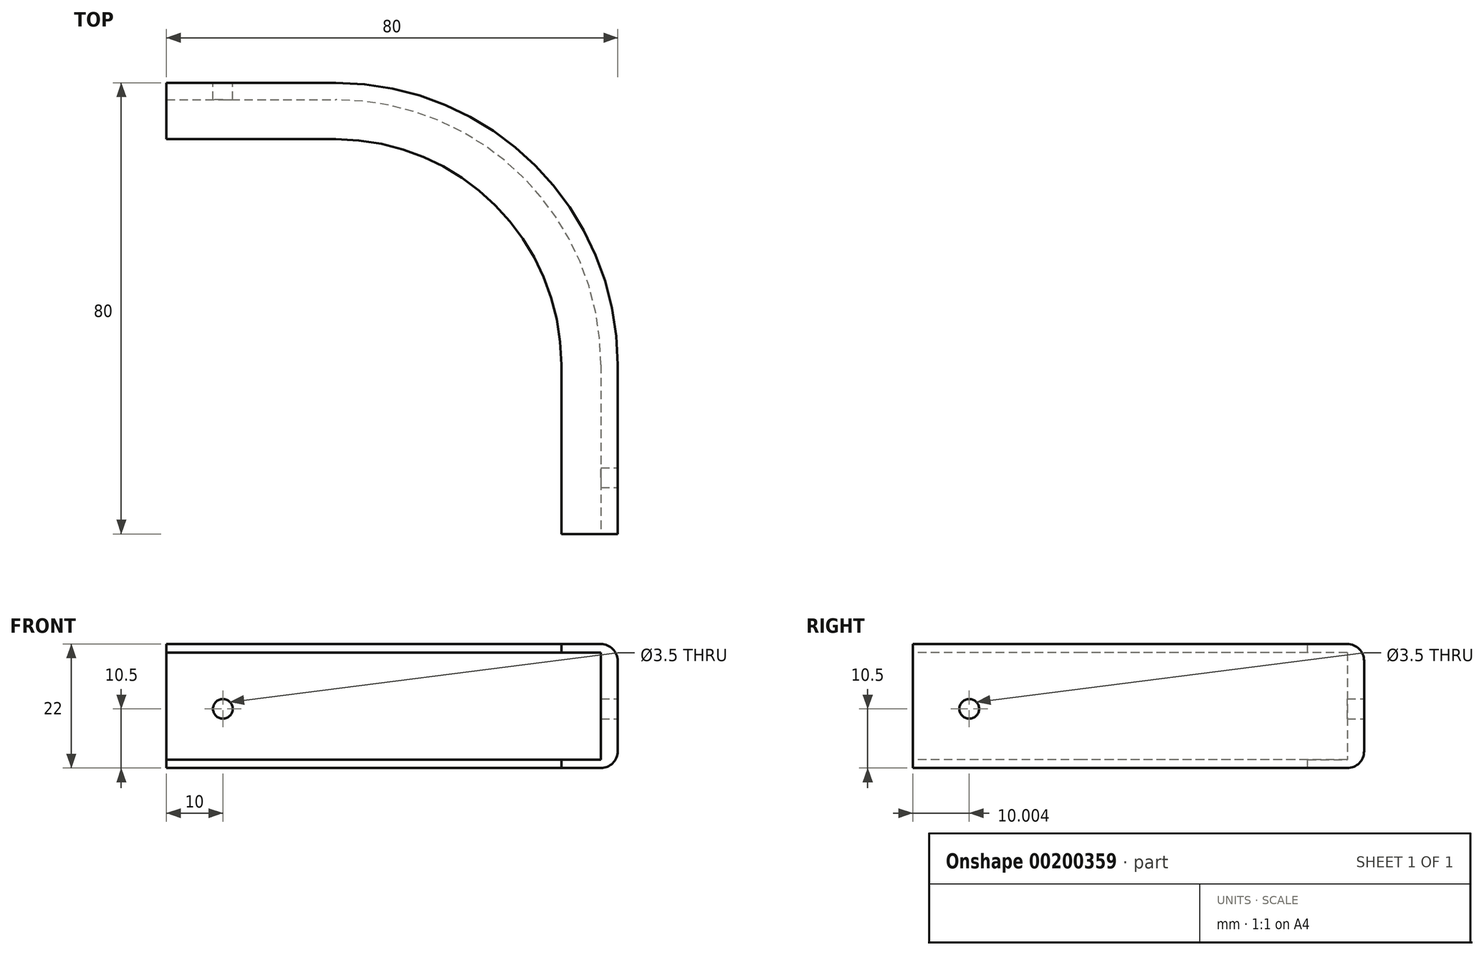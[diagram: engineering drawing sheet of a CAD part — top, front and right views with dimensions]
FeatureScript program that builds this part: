
annotation { "Feature Type Name" : "Feature", "Feature Type Description" : "" }
export const myFeature = defineFeature(function(context is Context, id is Id, definition is map)
    precondition{}
    {
        {
            var Q0;
            Q0=qCreatedBy(makeId("Right.planeOp"),FACE);
            var sketch = newSketch(context, id + "F0", { "sketchPlane" : qUnion([Q0])});
            skPoint(sketch, "E0.0", {"position": v(1.08, 10) * mm});
            skPoint(sketch, "E1.0", {"position": v(1.08, -9) * mm});
            skLineSegment(sketch, "E2", {"start": v(1.08, 10) * mm, "end": v(-5.92, 10) * mm});
            skLineSegment(sketch, "E3", {"start": v(-5.92, 10) * mm, "end": v(-5.92, 11.5) * mm});
            skLineSegment(sketch, "E4", {"start": v(-5.92, 11.5) * mm, "end": v(1.08, 11.5) * mm});
            skLineSegment(sketch, "E5", {"start": v(4.08, 8.5) * mm, "end": v(4.08, -7.5) * mm});
            skLineSegment(sketch, "E6", {"start": v(1.08, -10.5) * mm, "end": v(-5.92, -10.5) * mm});
            skLineSegment(sketch, "E7", {"start": v(-5.92, -10.5) * mm, "end": v(-5.92, -9) * mm});
            skLineSegment(sketch, "E8", {"start": v(-5.92, -9) * mm, "end": v(1.08, -9) * mm});
            skLineSegment(sketch, "E9", {"start": v(1.08, 10) * mm, "end": v(1.08, -9) * mm});
            skPoint(sketch, "E10.visualSharp", {"position": v(4.08, 11.5) * mm});
            skArc(sketch, "E10.filletArc", {"start": v(4.08, 8.5) * mm, "mid": v(3.2, 10.62) * mm, "end": v(1.08, 11.5) * mm});
            skPoint(sketch, "E11.visualSharp", {"position": v(4.08, -10.5) * mm});
            skArc(sketch, "E11.filletArc", {"start": v(1.08, -10.5) * mm, "mid": v(3.2, -9.62) * mm, "end": v(4.08, -7.5) * mm});
            skSolve(sketch);
        }
        {
            var Q0;
            Q0=qCreatedBy(makeId("Top.planeOp"),FACE);
            var sketch = newSketch(context, id + "F1", { "sketchPlane" : qUnion([Q0])});
            skPoint(sketch, "E12.0", {"position": v(0, -5.92) * mm});
            skLineSegment(sketch, "E13", {"start": v(0, -5.92) * mm, "end": v(30, -5.92) * mm});
            skArc(sketch, "E14", {"start": v(30, -5.92) * mm, "mid": v(58.28, -17.63) * mm, "end": v(70, -45.92) * mm});
            skLineSegment(sketch, "E15", {"start": v(70, -45.92) * mm, "end": v(70, -75.92) * mm});
            skSolve(sketch);
        }
        {
            var Q0;
            Q0 = qSketchRegion(id + "F0", true);
            var Q1;
            Q1 = qConstructionFilter(qBodyType(qCreatedBy(id + "F1" ,EDGE), BodyType.WIRE), ConstructionObject.NO);
            sweep(context, id + "F2", {"profiles" : qUnion([Q0]), "path" : qUnion([Q1])});
        }
        {
            var Q0;
            Q0=makeQuery(id+"F2.opSweep","SWEPT_FACE",FACE,{"disambiguationData":[OSD([sQuery(id+"F0.wireOp",EDGE,"E5"),sQuery(id+"F1.wireOp",EDGE,"E15")])]});
            var sketch = newSketch(context, id + "F3", { "sketchPlane" : qUnion([Q0])});
            skCircle(sketch, "E16", {"center": v(-65.92, 0) * mm, "radius": 1.75 * mm});
            skSolve(sketch);
        }
        {
            var Q0;
            Q0 = qSketchRegion(id + "F3", true);
            extrude(context, id + "F4", {"entities" : qUnion([Q0]), "operationType" : NewBodyOperationType.REMOVE, "endBound" : BoundingType.UP_TO_NEXT, "oppositeDirection" : true, "depth" : 25 * mm});
        }
        {
            var Q0;
            Q0=makeQuery(id+"F2.opSweep","SWEPT_FACE",FACE,{"disambiguationData":[OSD([sQuery(id+"F0.wireOp",EDGE,"E5"),sQuery(id+"F1.wireOp",EDGE,"E13")])]});
            var sketch = newSketch(context, id + "F5", { "sketchPlane" : qUnion([Q0])});
            skCircle(sketch, "E17", {"center": v(-10, 0) * mm, "radius": 1.75 * mm});
            skSolve(sketch);
        }
        {
            var Q0;
            Q0 = qSketchRegion(id + "F5", true);
            extrude(context, id + "F6", {"entities" : qUnion([Q0]), "operationType" : NewBodyOperationType.REMOVE, "endBound" : BoundingType.UP_TO_NEXT, "oppositeDirection" : true, "depth" : 25 * mm});
        }
    });
